# Revit family: PRD_AR_ThrmsttcMxngVlvs_HygieneUnit_ACLX1005_ACLX1007
name_source: partatom
category: Specialty Equipment
units: mm (PartAtom-declared; Revit-internal decimal feet)

## family parameters
Cut with Voids When Loaded = Yes
Host = Face
OmniClass Number = 23.60.50.24
OmniClass Title = Electric Controls
Part Type = Normal
Room Calculation Point = No
Round Connector Dimension = Use Diameter
Shared = No

## types (2) — shared parameters
AssetType = Fixed
BodyMaterial = PRD_AR_SyntheticWhite
Category = Pr_65_54_95_88, Thermostatic mixing valves
CloseOffRating = 0.0 Pa
Default Elevation = 1219 mm
DurationUnit = year
IfcExportAs = IfcValveType
IfcExportType = USERDEFINED
IntegralAccessories = electronic control unit
Manufacturer = KWC Group AG
ManufacturerName = KWC Group AG
ManufacturerURL = www.kwc.com
NBSDescription = Thermostatic mixing valves
NBSReference = 90-10-90/370
PowerConsumption = 3 Voltampere
PowerSupplyConnection = 6,75 / 12 V DC / A3000 open
ProductInformation = http://pim.kwc.com
ProtectiveSystemIP = IP 67
Quantity = 1
QuantityUom = piece
Size = 0.000000000000
Status = New
TailorMade = no
TestPressure = 0.0 Pa
URL = www.kwc.com
Uniclass2015Code = Pr_65_54_95_88
Uniclass2015Title = Thermostatic mixing valves
Uniclass2015Version = Products v1.32
ValveMechanism = OTHER
ValveOperation = SOLENOID
ValvePattern = STRAIGHT_2_PORT
Version = 1
WarrantyDurationUnit = year
WorkingPressure = 0.0 Pa
zero-valued in all types: FlowCoefficient, NominalDepth, NominalHeight, NominalWidth

## per-type parameters (varying)
| type | BIMObjectName | Description | Features | ModelNumber | Name |
| ACLX1005 | PRD_AR_ThermostaticMixingValves_HygieneUnit_ACLX1005 | Hygiene unit for F5L single lever mixer, projection 100 mm, for performing automatic hygiene flushing and program-controlled thermal disinfection. Function block with 2 solenoid valve cartridges and an electronic control unit for installation in walls with flush box and cover made of plastic 150 x 80 mm, for battery or mains operation, 6 V DC. Activated water hygiene flushing, fixed interval of 24 hours and saving of statistical data. With option for parameterization and communication via optional, bidirectional remote control. Battery compartment including battery or in-wall power supply unit must be ordered separately. | projection 100 mm, for performing automatic hygiene flushing and program-controlled thermal disinfection. Battery compartment including battery or in-wall power supply unit must be ordered separately. | 2030068987 | Hygiene unit ACLX1005 |
| ACLX1007 | PRD_AR_ThermostaticMixingValves_HygieneUnit_ACLX1007 | Hygiene unit for F5L single lever mixer, projection 125 mm, for performing automatic hygiene flushing and program-controlled thermal disinfection. Function block with 2 solenoid valve cartridges and an electronic control unit for installation in walls with flush box and cover made of plastic 150 x 80 mm, for battery or mains operation, 6 V DC. Activated water hygiene flushing, fixed interval of 24 hours and saving of statistical data. With option for parameterization and communication via optional, bidirectional remote control. Battery compartment including battery or in-wall power supply unit must be ordered separately. | projection 125 mm, for performing automatic hygiene flushing and program-controlled thermal disinfection. Battery compartment including battery or in-wall power supply unit must be ordered separately. | 2030068988 | Hygiene unit ACLX1007 |

note: column(s) folded — value = type name in every type: Model, ModelReference

## geometry (parser evidence)
native form markers: Sweep x3
no freeform markers — native parametric forms only
